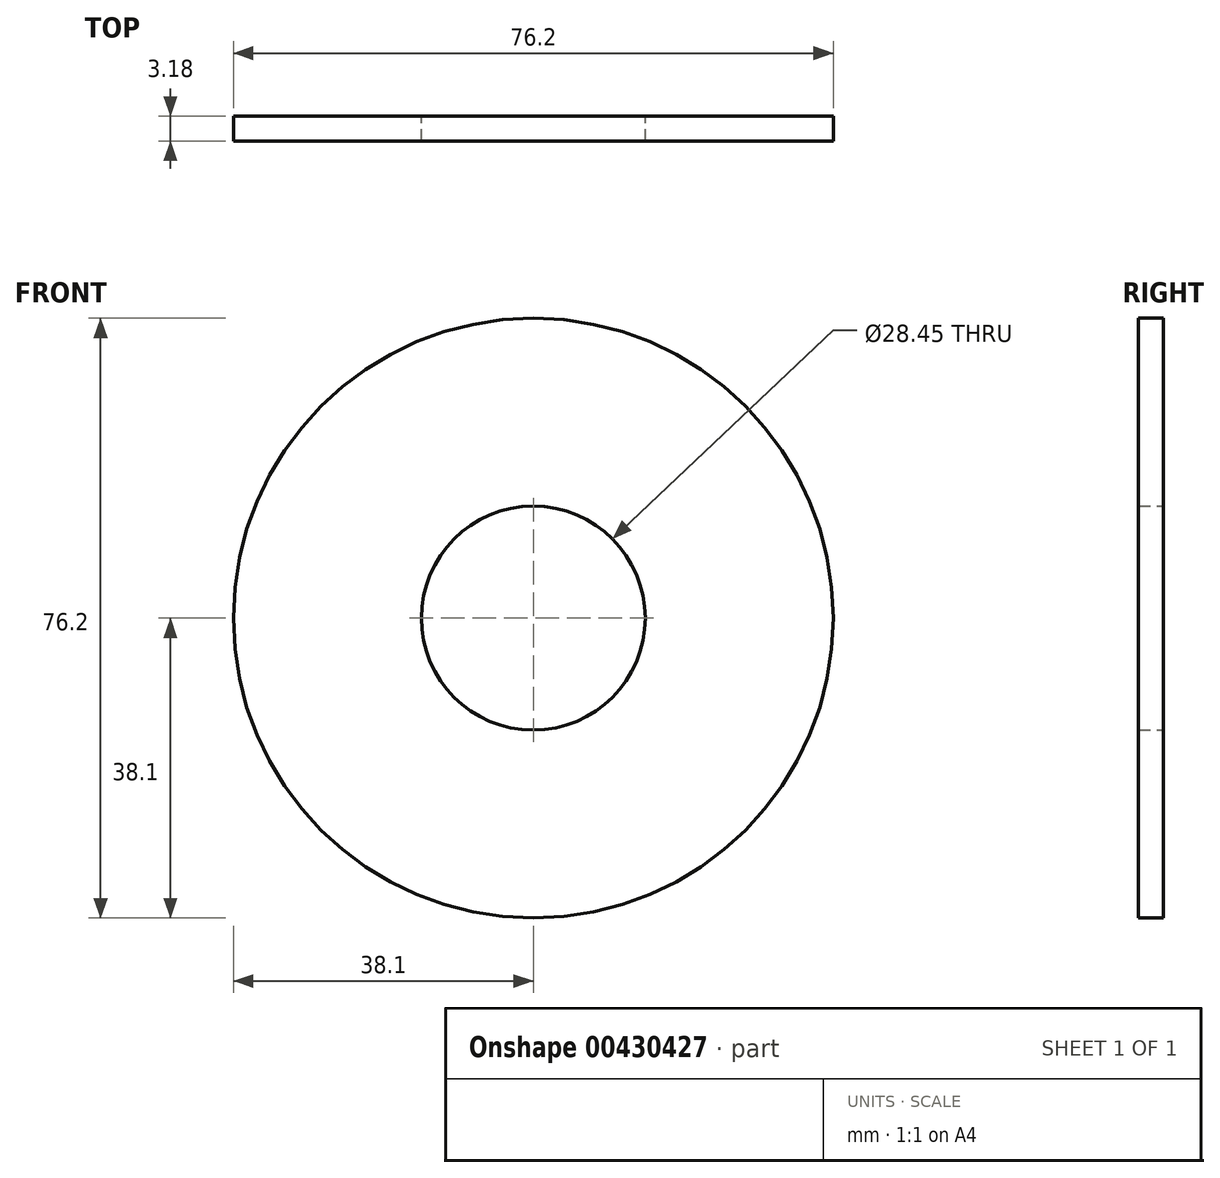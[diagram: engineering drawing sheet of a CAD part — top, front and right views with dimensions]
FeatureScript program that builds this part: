
annotation { "Feature Type Name" : "Feature", "Feature Type Description" : "" }
export const myFeature = defineFeature(function(context is Context, id is Id, definition is map)
    precondition{}
    {
        {
            var Q0;
            Q0=qCreatedBy(makeId("Front.planeOp"),FACE);
            var sketch = newSketch(context, id + "F0", { "sketchPlane" : qUnion([Q0])});
            skLineSegment(sketch, "E0.4", {"start": v(0, 0) * mm, "end": v(0, 0) * mm});
            skCircle(sketch, "E1", {"center": v(0, 0) * mm, "radius": 38.1 * mm});
            skCircle(sketch, "E2", {"center": v(0, 0) * mm, "radius": 14.22 * mm});
            skSolve(sketch);
        }
        {
            var Q0;
            Q0 = qSketchRegion(id + "F0", true);
            extrude(context, id + "F1", {"entities" : qUnion([Q0]), "depth" : 3.17 * mm, "offsetDistance" : 25.4 * mm});
        }
    });
